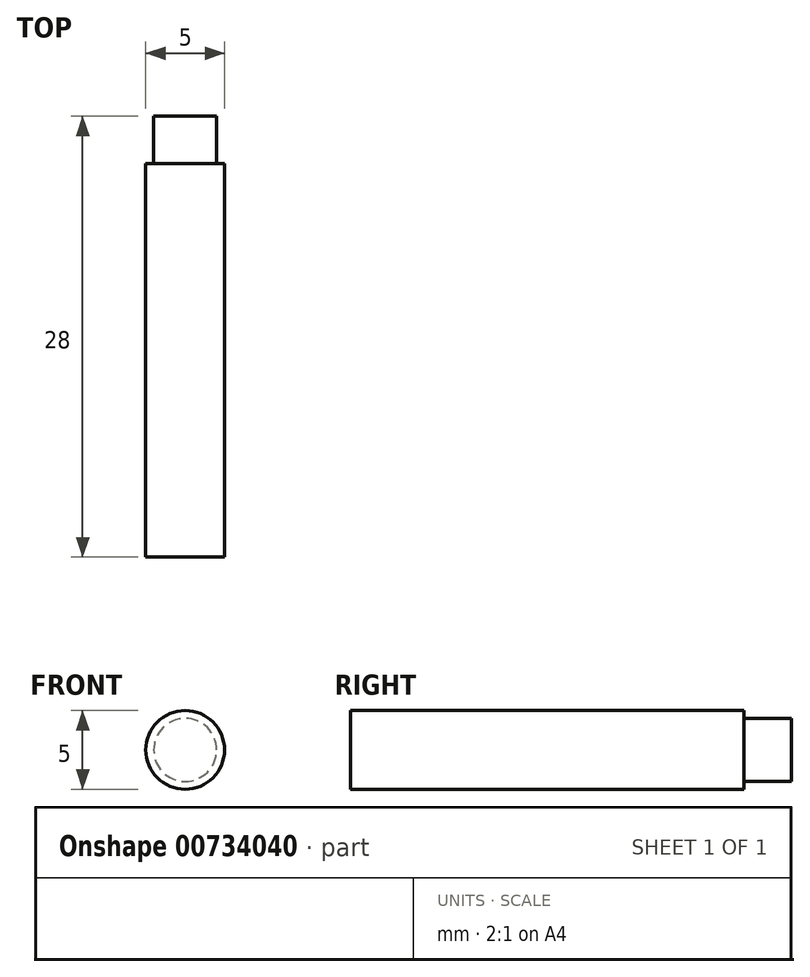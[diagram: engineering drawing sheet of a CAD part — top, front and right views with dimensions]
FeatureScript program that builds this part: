
annotation { "Feature Type Name" : "Feature", "Feature Type Description" : "" }
export const myFeature = defineFeature(function(context is Context, id is Id, definition is map)
    precondition{}
    {
        {
            var Q0;
            Q0=qCreatedBy(makeId("Front.planeOp"),FACE);
            var sketch = newSketch(context, id + "F0", { "sketchPlane" : qUnion([Q0])});
            skCircle(sketch, "E0", {"center": v(0, 0) * mm, "radius": 2.5 * mm});
            skSolve(sketch);
        }
        {
            var Q0;
            Q0=qSketchRegion(id+"F0",true);
            extrude(context, id + "F1", {"entities" : qUnion([Q0]), "depth" : 25 * mm, "offsetDistance" : 25 * mm});
        }
        {
            var Q0;
            Q0=makeQuery(id+"F1.opExtrude","CAP_FACE",FACE,{"disambiguationData":[OSD([sQuery(id+"F0.wireOp",EDGE,"E0")])],"isStart":true});
            var sketch = newSketch(context, id + "F2", { "sketchPlane" : qUnion([Q0])});
            skCircle(sketch, "E1", {"center": v(0, 0) * mm, "radius": 2 * mm});
            skSolve(sketch);
        }
        {
            var Q0;
            Q0=qSketchRegion(id+"F2",true);
            extrude(context, id + "F3", {"entities" : qUnion([Q0]), "operationType" : NewBodyOperationType.ADD, "depth" : 3 * mm, "offsetDistance" : 25 * mm});
        }
    });
